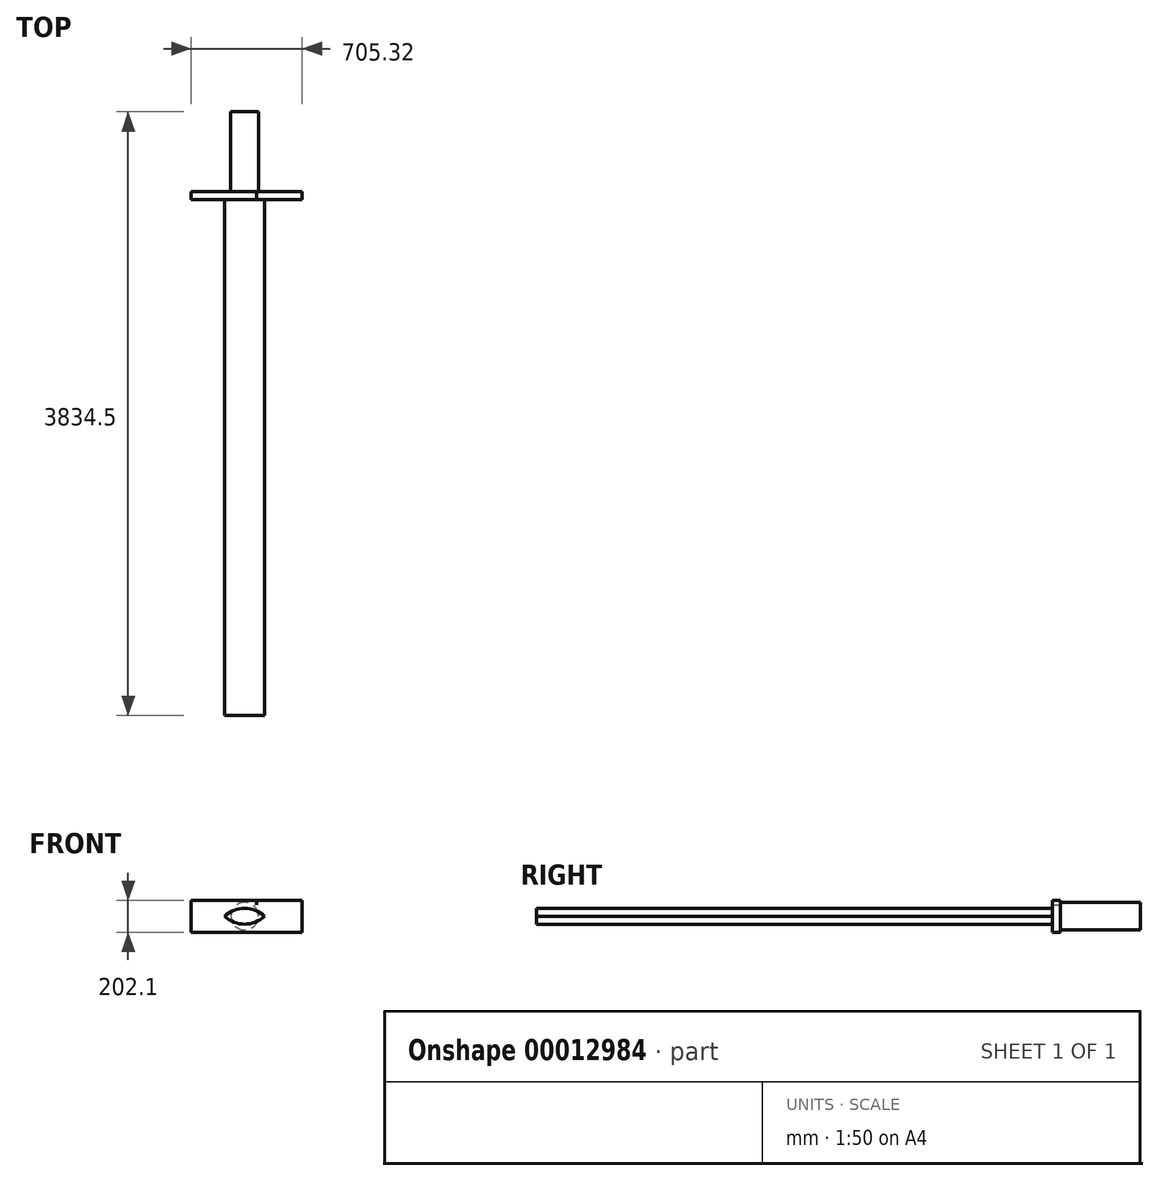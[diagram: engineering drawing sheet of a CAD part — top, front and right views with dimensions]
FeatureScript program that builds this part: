
annotation { "Feature Type Name" : "Feature", "Feature Type Description" : "" }
export const myFeature = defineFeature(function(context is Context, id is Id, definition is map)
    precondition{}
    {
        {
            var Q0;
            Q0=qCreatedBy(makeId("Front.planeOp"),FACE);
            var sketch = newSketch(context, id + "F4", { "sketchPlane" : qUnion([Q0])});
            skCircle(sketch, "E0", {"center": v(0, 0) * mm, "radius": 87.85 * mm});
            skSolve(sketch);
        }
        {
            var Q0;
            Q0=qCreatedBy(makeId("Front.planeOp"),FACE);
            var sketch = newSketch(context, id + "F0", { "sketchPlane" : qUnion([Q0])});
            skLineSegment(sketch, "E1.bottom", {"start": v(75.7, 99.94) * mm, "end": v(74.82, 99.94) * mm});
            skLineSegment(sketch, "E1.top", {"start": v(75.7, 71.21) * mm, "end": v(74.82, 71.21) * mm});
            skLineSegment(sketch, "E1.left", {"start": v(75.7, 99.94) * mm, "end": v(75.7, 71.21) * mm});
            skLineSegment(sketch, "E1.right", {"start": v(74.82, 99.94) * mm, "end": v(74.82, 71.21) * mm});
            skLineSegment(sketch, "E2.bottom", {"start": v(-338.76, -102.16) * mm, "end": v(366.56, -102.16) * mm});
            skLineSegment(sketch, "E2.top", {"start": v(-338.76, 99.94) * mm, "end": v(366.56, 99.94) * mm});
            skLineSegment(sketch, "E2.left", {"start": v(-338.76, -102.16) * mm, "end": v(-338.76, 99.94) * mm});
            skLineSegment(sketch, "E2.right", {"start": v(366.56, -102.16) * mm, "end": v(366.56, 99.94) * mm});
            skSolve(sketch);
        }
        {
            var Q0;
            Q0=makeQuery(id+"F0.imprint","IMPRINT",FACE,{"disambiguationData":[TD([[makeQuery(id+"F0.imprint","IMPRINT",EDGE,{"derivedFrom":sQuery(id+"F0.wireOp",EDGE,"E1.top")}),1.0]])]});
            extrude(context, id + "F5", {"entities" : qUnion([Q0]), "depth" : 50.8 * mm});
        }
        {
            var Q0;
            Q0=makeQuery(id+"F4.imprint","IMPRINT",FACE,{"disambiguationData":[TD([[makeQuery(id+"F4.imprint","IMPRINT",EDGE,{"derivedFrom":sQuery(id+"F4.wireOp",EDGE,"E0")}),1.0]])]});
            extrude(context, id + "F1", {"entities" : qUnion([Q0]), "operationType" : NewBodyOperationType.ADD, "oppositeDirection" : true, "depth" : 508 * mm});
        }
        {
            var Q0;
            Q0=makeQuery(id+"F5.opExtrude","CAP_FACE",FACE,{"disambiguationData":[OSD([sQuery(id+"F0.wireOp",EDGE,"E1.top"),sQuery(id+"F0.wireOp",EDGE,"E1.left"),sQuery(id+"F0.wireOp",EDGE,"E1.right"),sQuery(id+"F0.wireOp",EDGE,"E2.bottom"),sQuery(id+"F0.wireOp",EDGE,"E2.top"),sQuery(id+"F0.wireOp",EDGE,"E2.left"),sQuery(id+"F0.wireOp",EDGE,"E2.right")])],"isStart":false});
            var sketch = newSketch(context, id + "F2", { "sketchPlane" : qUnion([Q0])});
            skArc(sketch, "E3", {"start": v(-127, 0) * mm, "mid": v(0, -50.8) * mm, "end": v(127, 0) * mm});
            skArc(sketch, "E4", {"start": v(127, 0) * mm, "mid": v(0, 50.8) * mm, "end": v(-127, 0) * mm});
            skSolve(sketch);
        }
        {
            var Q0;
            Q0=makeQuery(id+"F2.imprint","IMPRINT",FACE,{"disambiguationData":[TD([[makeQuery(id+"F2.imprint","IMPRINT",EDGE,{"derivedFrom":sQuery(id+"F2.wireOp",EDGE,"E3")}),1.0]])]});
            extrude(context, id + "F6", {"entities" : qUnion([Q0]), "operationType" : NewBodyOperationType.ADD, "depth" : 3275.7 * mm});
        }
    });
